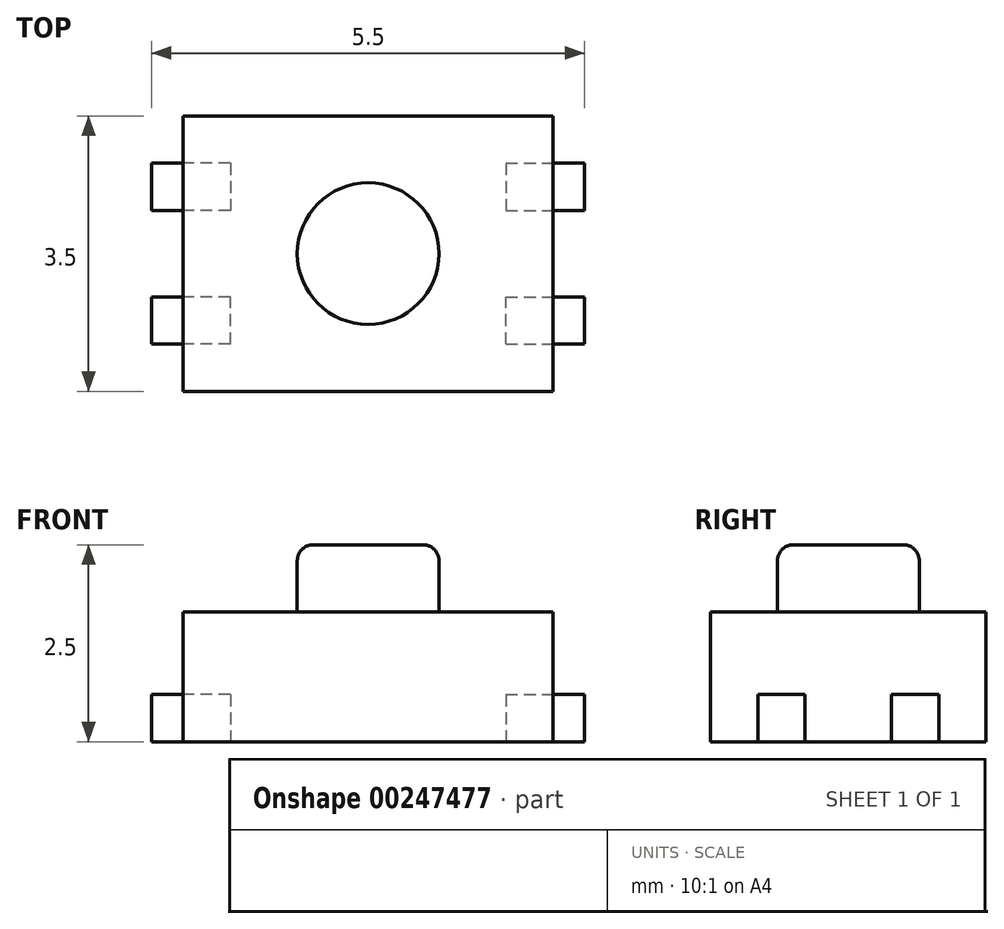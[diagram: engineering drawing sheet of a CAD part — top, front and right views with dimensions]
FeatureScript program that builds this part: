
annotation { "Feature Type Name" : "Feature", "Feature Type Description" : "" }
export const myFeature = defineFeature(function(context is Context, id is Id, definition is map)
    precondition{}
    {
        {
            var Q0;
            Q0=qCreatedBy(makeId("Top.planeOp"),FACE);
            var sketch = newSketch(context, id + "F0", { "sketchPlane" : qUnion([Q0])});
            skLineSegment(sketch, "E0.bottom", {"start": v(2.35, -1.75) * mm, "end": v(-2.35, -1.75) * mm});
            skLineSegment(sketch, "E0.top", {"start": v(2.35, 1.75) * mm, "end": v(-2.35, 1.75) * mm});
            skLineSegment(sketch, "E0.left", {"start": v(2.35, -1.75) * mm, "end": v(2.35, 1.75) * mm});
            skLineSegment(sketch, "E0.right", {"start": v(-2.35, -1.75) * mm, "end": v(-2.35, 1.75) * mm});
            skPoint(sketch, "E0.middle", {"position": v(0, 0) * mm});
            skSolve(sketch);
        }
        {
            var Q0;
            Q0 = qSketchRegion(id + "F0", true);
            extrude(context, id + "F1", {"entities" : qUnion([Q0]), "depth" : 1.65 * mm});
        }
        {
            var Q0;
            Q0=makeQuery(id+"F1.opExtrude","CAP_FACE",FACE,{"disambiguationData":[OSD([sQuery(id+"F0.wireOp",EDGE,"E0.bottom"),sQuery(id+"F0.wireOp",EDGE,"E0.top"),sQuery(id+"F0.wireOp",EDGE,"E0.left"),sQuery(id+"F0.wireOp",EDGE,"E0.right")])],"isStart":true});
            var sketch = newSketch(context, id + "F2", { "sketchPlane" : qUnion([Q0])});
            skLineSegment(sketch, "E1", {"start": v(0, 0) * mm, "end": v(-4.17, 0) * mm, "construction": true});
            skPoint(sketch, "E1.endSnap0", {"position": v(-2.35, 0) * mm});
            skLineSegment(sketch, "E2", {"start": v(0, 0) * mm, "end": v(0, 2.18) * mm, "construction": true});
            skPoint(sketch, "E2.endSnap0", {"position": v(0, 1.75) * mm});
            skLineSegment(sketch, "E3.bottom", {"start": v(-1.75, 1.15) * mm, "end": v(-2.75, 1.15) * mm});
            skLineSegment(sketch, "E3.top", {"start": v(-1.75, 0.55) * mm, "end": v(-2.75, 0.55) * mm});
            skLineSegment(sketch, "E3.left", {"start": v(-1.75, 1.15) * mm, "end": v(-1.75, 0.55) * mm});
            skLineSegment(sketch, "E3.right", {"start": v(-2.75, 1.15) * mm, "end": v(-2.75, 0.55) * mm});
            skLineSegment(sketch, "E4.MirrorCS", {"start": v(2.75, 1.15) * mm, "end": v(2.75, 0.55) * mm});
            skLineSegment(sketch, "E5.MirrorCS", {"start": v(1.75, 1.15) * mm, "end": v(1.75, 0.55) * mm});
            skLineSegment(sketch, "E6.MirrorCS", {"start": v(1.75, 0.55) * mm, "end": v(2.75, 0.55) * mm});
            skLineSegment(sketch, "E7.MirrorCS", {"start": v(1.75, 1.15) * mm, "end": v(2.75, 1.15) * mm});
            skLineSegment(sketch, "E8.MirrorCS", {"start": v(0, 0) * mm, "end": v(4.17, 0) * mm, "construction": true});
            skPoint(sketch, "E9.MirrorP", {"position": v(2.35, 0) * mm});
            skLineSegment(sketch, "E10.MirrorCS", {"start": v(2.75, -1.15) * mm, "end": v(2.75, -0.55) * mm});
            skLineSegment(sketch, "E11.MirrorCS", {"start": v(-1.75, -1.15) * mm, "end": v(-2.75, -1.15) * mm});
            skLineSegment(sketch, "E12.MirrorCS", {"start": v(-1.75, -0.55) * mm, "end": v(-2.75, -0.55) * mm});
            skLineSegment(sketch, "E13.MirrorCS", {"start": v(1.75, -1.15) * mm, "end": v(1.75, -0.55) * mm});
            skLineSegment(sketch, "E14.MirrorCS", {"start": v(1.75, -0.55) * mm, "end": v(2.75, -0.55) * mm});
            skLineSegment(sketch, "E15.MirrorCS", {"start": v(1.75, -1.15) * mm, "end": v(2.75, -1.15) * mm});
            skLineSegment(sketch, "E16.MirrorCS", {"start": v(-2.75, -1.15) * mm, "end": v(-2.75, -0.55) * mm});
            skLineSegment(sketch, "E17.MirrorCS", {"start": v(-1.75, -1.15) * mm, "end": v(-1.75, -0.55) * mm});
            skSolve(sketch);
        }
        {
            var Q0;
            Q0 = qSketchRegion(id + "F2", true);
            extrude(context, id + "F3", {"entities" : qUnion([Q0]), "oppositeDirection" : true, "depth" : .6 * mm});
        }
        {
            var Q0;
            Q0=makeQuery(id+"F1.opExtrude","CAP_FACE",FACE,{"disambiguationData":[OSD([sQuery(id+"F0.wireOp",EDGE,"E0.bottom"),sQuery(id+"F0.wireOp",EDGE,"E0.top"),sQuery(id+"F0.wireOp",EDGE,"E0.left"),sQuery(id+"F0.wireOp",EDGE,"E0.right")])],"isStart":false});
            var sketch = newSketch(context, id + "F4", { "sketchPlane" : qUnion([Q0])});
            skCircle(sketch, "E18", {"center": v(0, 0) * mm, "radius": 0.9 * mm});
            skSolve(sketch);
        }
        {
            var Q0;
            Q0 = qSketchRegion(id + "F4", true);
            extrude(context, id + "F5", {"entities" : qUnion([Q0]), "depth" : (2.5 - 1.65) * mm});
        }
        {
            var Q0;
            Q0=makeQuery(id+"F5.opExtrude","CAP_EDGE",EDGE,{"disambiguationData":[OSD([sQuery(id+"F4.wireOp",EDGE,"E18")])],"isStart":false});
            fillet(context, id + "F6", {"entities" : qUnion([Q0]), "radius" : .2 * mm, "tangentPropagation" : true, "allowEdgeOverflow" : false});
        }
    });
